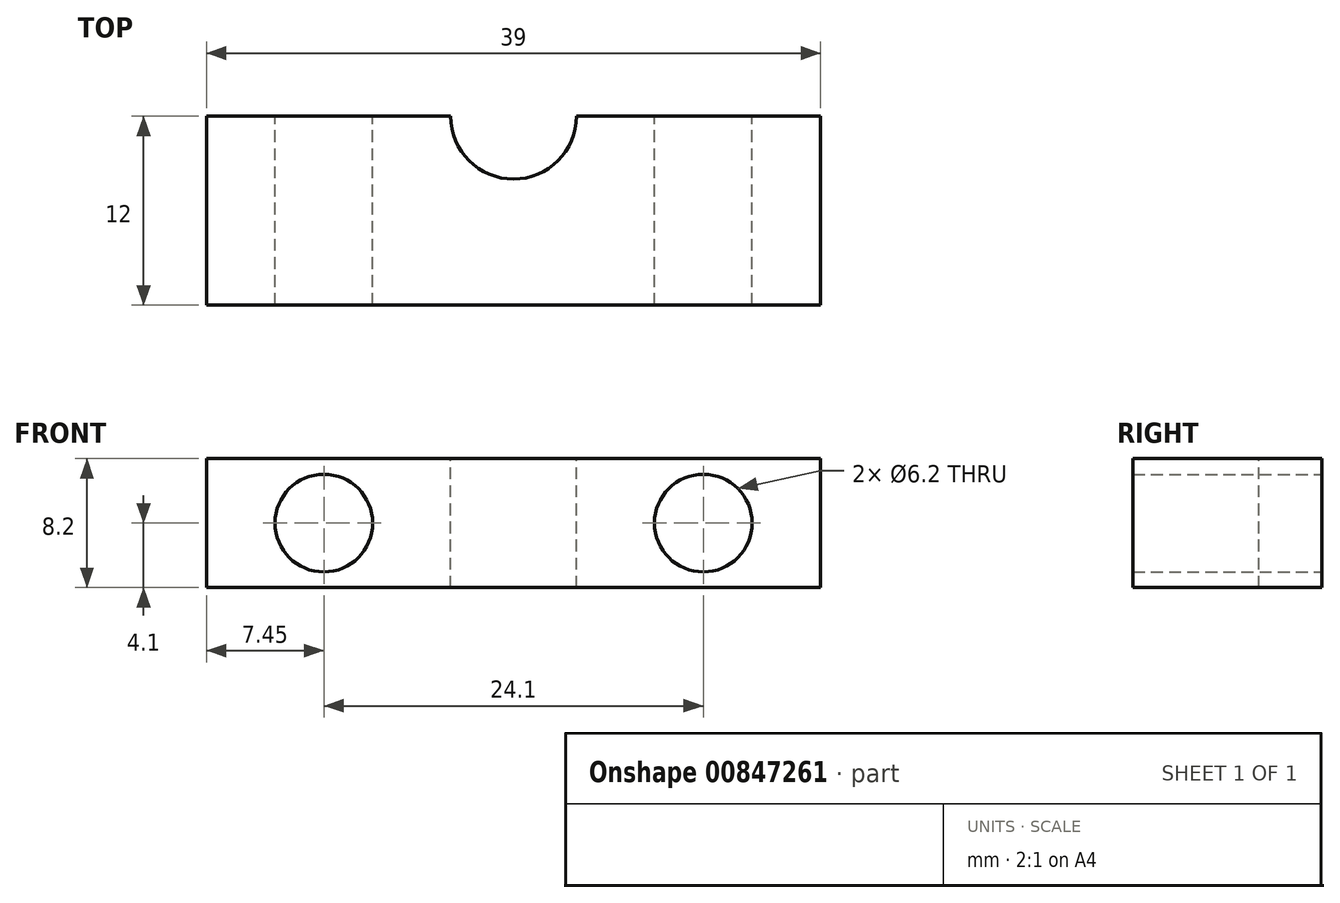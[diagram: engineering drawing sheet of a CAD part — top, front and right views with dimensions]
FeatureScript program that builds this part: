
annotation { "Feature Type Name" : "Feature", "Feature Type Description" : "" }
export const myFeature = defineFeature(function(context is Context, id is Id, definition is map)
    precondition{}
    {
        {
            var Q0;
            Q0=qCreatedBy(makeId("Front.planeOp"),FACE);
            var sketch = newSketch(context, id + "F0", { "sketchPlane" : qUnion([Q0])});
            skLineSegment(sketch, "E0.bottom", {"start": v(-19.5, -4.1) * mm, "end": v(19.5, -4.1) * mm});
            skLineSegment(sketch, "E0.top", {"start": v(-19.5, 4.1) * mm, "end": v(19.5, 4.1) * mm});
            skLineSegment(sketch, "E0.left", {"start": v(-19.5, -4.1) * mm, "end": v(-19.5, 4.1) * mm});
            skLineSegment(sketch, "E0.right", {"start": v(19.5, -4.1) * mm, "end": v(19.5, 4.1) * mm});
            skPoint(sketch, "E0.middle", {"position": v(0, 0) * mm});
            skLineSegment(sketch, "E1.bottom", {"start": v(-60.89, 7.08) * mm, "end": v(-61.51, 7.08) * mm});
            skLineSegment(sketch, "E1.top", {"start": v(-60.89, 3.96) * mm, "end": v(-61.51, 3.96) * mm});
            skLineSegment(sketch, "E1.left", {"start": v(-60.89, 7.08) * mm, "end": v(-60.89, 3.96) * mm});
            skLineSegment(sketch, "E1.right", {"start": v(-61.51, 7.08) * mm, "end": v(-61.51, 3.96) * mm});
            skPoint(sketch, "E1.middle", {"position": v(-61.2, 5.52) * mm});
            skCircle(sketch, "E2", {"center": v(-12.05, 0) * mm, "radius": 3.1 * mm});
            skCircle(sketch, "E3", {"center": v(12.05, 0) * mm, "radius": 3.1 * mm});
            skLineSegment(sketch, "E4", {"start": v(19.5, 4.1) * mm, "end": v(19.5, -4.1) * mm});
            skLineSegment(sketch, "E5", {"start": v(-12.05, 0) * mm, "end": v(12.05, 0) * mm});
            skSolve(sketch);
        }
        {
            var Q0;
            Q0=makeQuery(id+"F0.imprint","IMPRINT",FACE,{"disambiguationData":[TD([[makeQuery(id+"F0.imprint","IMPRINT",EDGE,{"derivedFrom":sQuery(id+"F0.wireOp",EDGE,"E0.bottom")}),1.0]])]});
            extrude(context, id + "F1", {"entities" : qUnion([Q0]), "flatOperationType" : FlatOperationType.REMOVE, "depth" : 12 * mm, "offsetDistance" : 25 * mm, "domain" : OperationDomain.MODEL});
        }
        {
            var Q0;
            Q0=makeQuery(id+"F1.opExtrude","SWEPT_FACE",FACE,{"disambiguationData":[OSD([sQuery(id+"F0.wireOp",EDGE,"E0.top")])]});
            var sketch = newSketch(context, id + "F2", { "sketchPlane" : qUnion([Q0])});
            skCircle(sketch, "E6", {"center": v(0, 0) * mm, "radius": 4 * mm});
            skSolve(sketch);
        }
        {
            var Q0;
            {var subQ0=sQuery(id+"F2.wireOp",EDGE,"E6");var subQ1=makeQuery(id+"F1.opExtrude","CAP_EDGE",EDGE,{"disambiguationData":[OSD([sQuery(id+"F0.wireOp",EDGE,"E0.top")])],"isStart":true});var subQ2=makeQuery(id+"F2.imprint","INTERSECT",VERTEX,{"disambiguationData":[OD(0.0)],"derivedFrom":[subQ1,subQ0]});Q0=makeQuery(id+"F2.imprint","IMPRINT",FACE,{"disambiguationData":[TD([[makeQuery(id+"F2.imprint","IMPRINT",EDGE,{"disambiguationData":[TD([[subQ2,-1.0]])],"derivedFrom":subQ0}),1.0]])]});}
            extrude(context, id + "F3", {"entities" : qUnion([Q0]), "operationType" : NewBodyOperationType.REMOVE, "oppositeDirection" : true, "depth" : 25 * mm, "offsetDistance" : 25 * mm});
        }
    });
